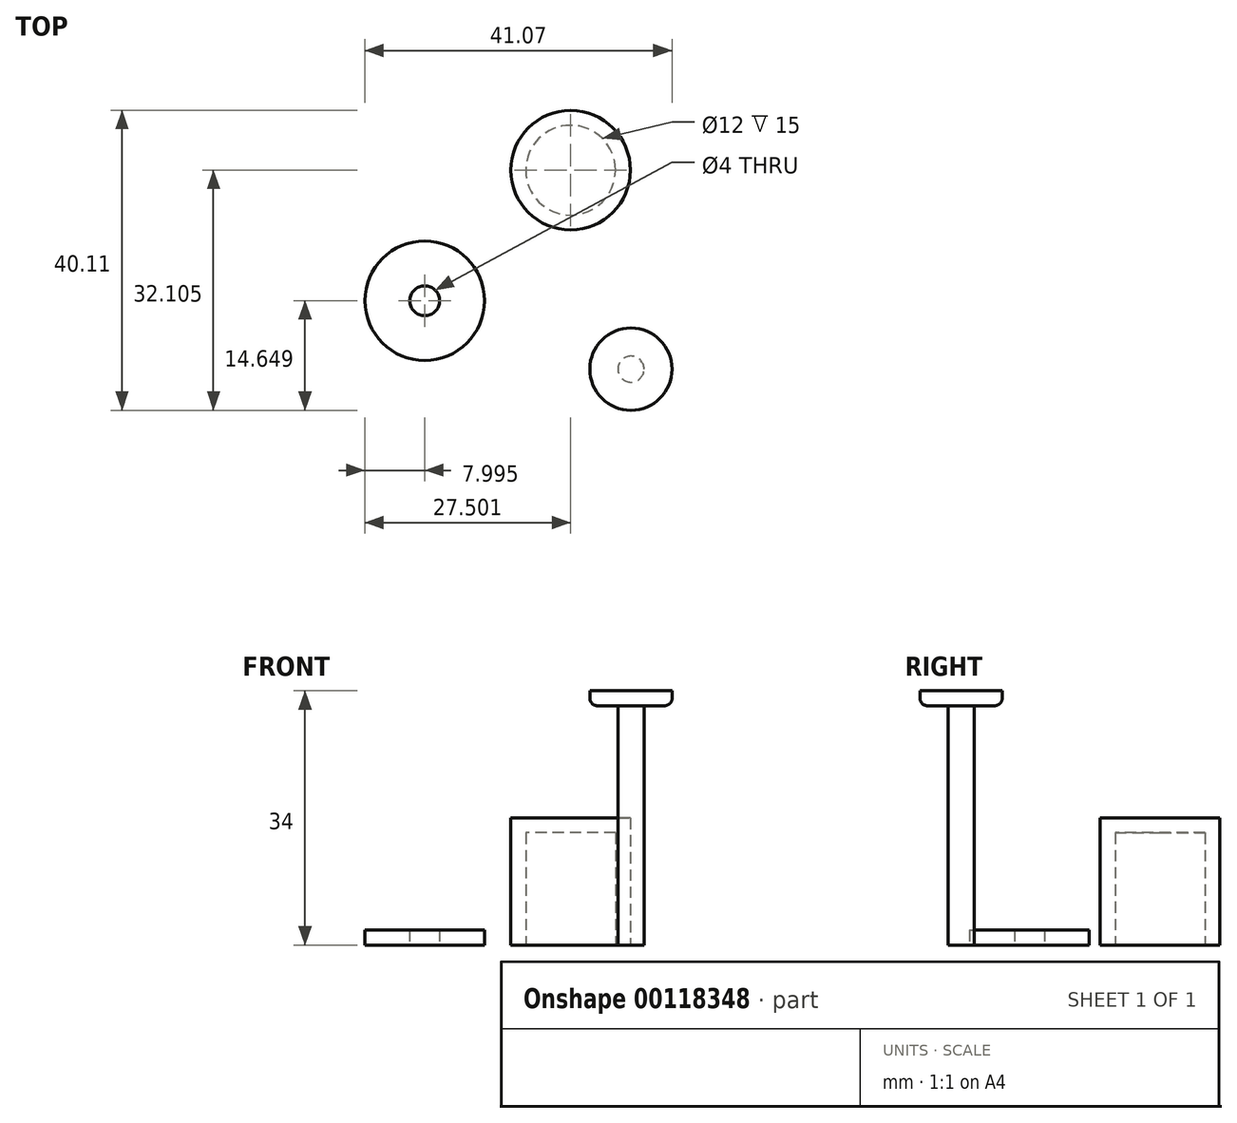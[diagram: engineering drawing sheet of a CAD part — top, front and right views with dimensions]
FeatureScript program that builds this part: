
annotation { "Feature Type Name" : "Feature", "Feature Type Description" : "" }
export const myFeature = defineFeature(function(context is Context, id is Id, definition is map)
    precondition{}
    {
        {
            var Q0;
            Q0=qCreatedBy(makeId("Top.planeOp"),FACE);
            var sketch = newSketch(context, id + "F0", { "sketchPlane" : qUnion([Q0])});
            skCircle(sketch, "E0", {"center": v(-41.52, 19.67) * mm, "radius": 8 * mm});
            skCircle(sketch, "E1", {"center": v(-41.52, 19.67) * mm, "radius": 2 * mm});
            skSolve(sketch);
        }
        {
            var Q0;
            Q0 = qSketchRegion(id + "F0", true);
            extrude(context, id + "F1", {"entities" : qUnion([Q0]), "depth" : 2 * mm});
        }
        {
            var Q0;
            Q0=qCreatedBy(makeId("Top.planeOp"),FACE);
            var sketch = newSketch(context, id + "F2", { "sketchPlane" : qUnion([Q0])});
            skCircle(sketch, "E2", {"center": v(-22.02, 37.13) * mm, "radius": 8 * mm});
            skCircle(sketch, "E3", {"center": v(-22.02, 37.13) * mm, "radius": 6 * mm});
            skSolve(sketch);
        }
        {
            var Q0;
            Q0 = qSketchRegion(id + "F2", true);
            extrude(context, id + "F3", {"entities" : qUnion([Q0]), "depth" : 15 * mm});
        }
        {
            var Q0;
            Q0=makeQuery(id+"F3.opExtrude","CAP_FACE",FACE,{"disambiguationData":[OSD([sQuery(id+"F2.wireOp",EDGE,"E2"),sQuery(id+"F2.wireOp",EDGE,"E3")])],"isStart":false});
            var sketch = newSketch(context, id + "F4", { "sketchPlane" : qUnion([Q0])});
            skCircle(sketch, "E4", {"center": v(-22.02, 37.13) * mm, "radius": 8 * mm});
            skSolve(sketch);
        }
        {
            var Q0;
            Q0 = qSketchRegion(id + "F4", true);
            extrude(context, id + "F5", {"entities" : qUnion([Q0]), "operationType" : NewBodyOperationType.ADD, "depth" : 2 * mm});
        }
        {
            var Q0;
            Q0=qCreatedBy(makeId("Top.planeOp"),FACE);
            var sketch = newSketch(context, id + "F6", { "sketchPlane" : qUnion([Q0])});
            skCircle(sketch, "E5", {"center": v(-13.95, 10.52) * mm, "radius": 1.75 * mm});
            skSolve(sketch);
        }
        {
            var Q0;
            Q0 = qSketchRegion(id + "F6", true);
            extrude(context, id + "F7", {"entities" : qUnion([Q0]), "depth" : 32 * mm});
        }
        {
            var Q0;
            Q0=makeQuery(id+"F7.opExtrude","CAP_FACE",FACE,{"disambiguationData":[OSD([sQuery(id+"F6.wireOp",EDGE,"E5")])],"isStart":false});
            var sketch = newSketch(context, id + "F8", { "sketchPlane" : qUnion([Q0])});
            skCircle(sketch, "E6", {"center": v(-13.95, 10.52) * mm, "radius": 5.5 * mm});
            skSolve(sketch);
        }
        {
            var Q0;
            Q0 = qSketchRegion(id + "F8", true);
            extrude(context, id + "F9", {"entities" : qUnion([Q0]), "operationType" : NewBodyOperationType.ADD, "depth" : 2 * mm});
        }
        {
            var Q0;
            Q0=makeQuery(id+"F9.opExtrude","CAP_EDGE",EDGE,{"disambiguationData":[OSD([sQuery(id+"F8.wireOp",EDGE,"E6")])],"isStart":true});
            fillet(context, id + "F10", {"entities" : qUnion([Q0]), "radius" : 1 * mm, "tangentPropagation" : true, "allowEdgeOverflow" : false});
        }
    });
